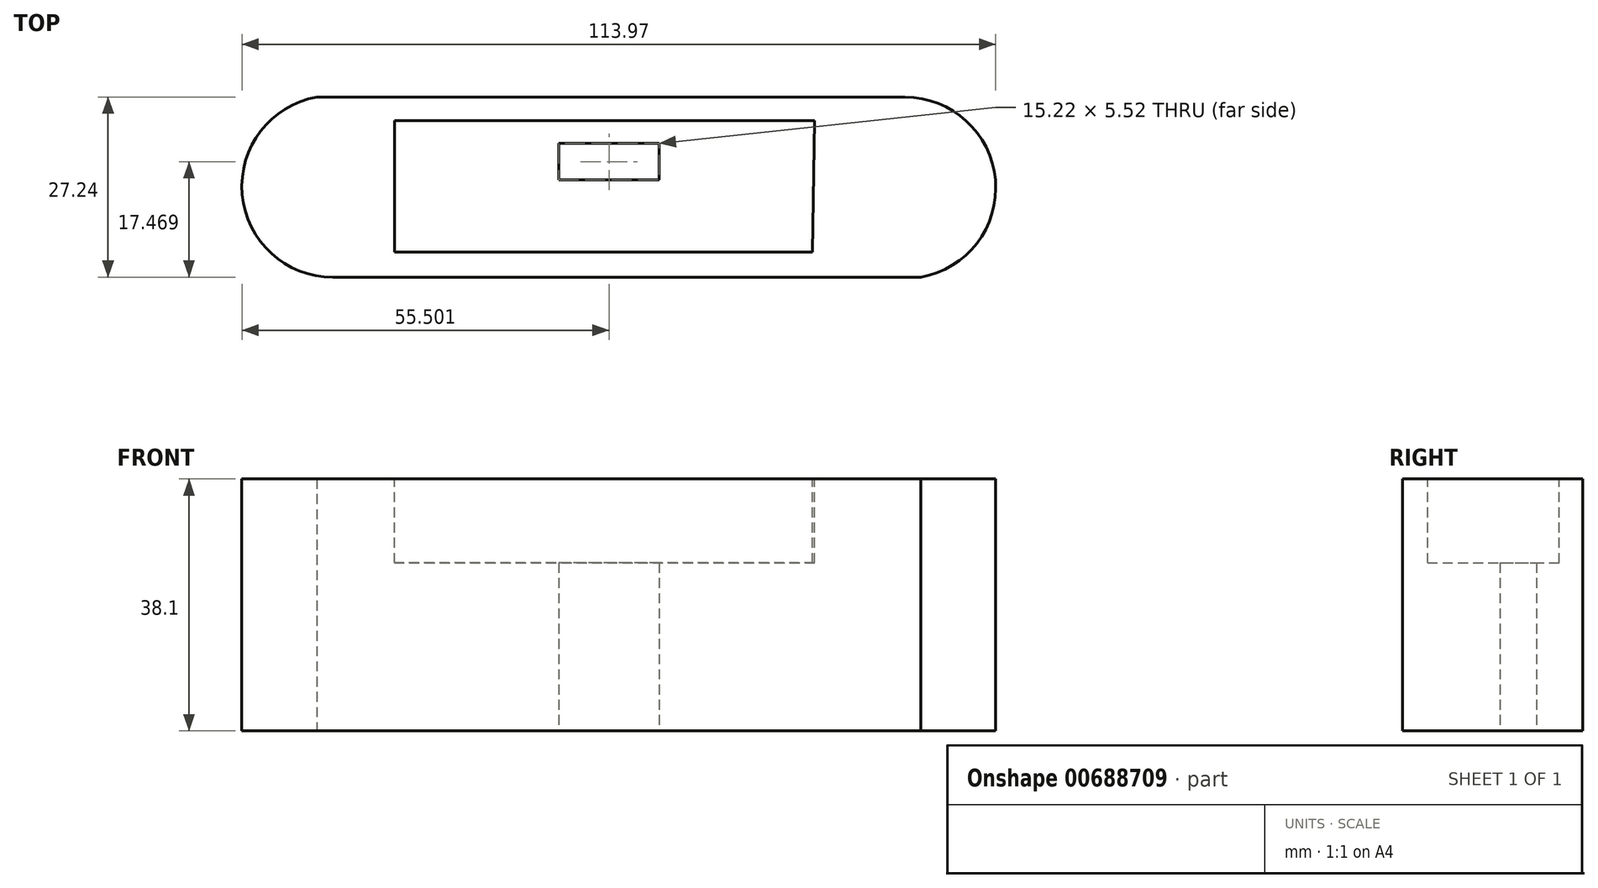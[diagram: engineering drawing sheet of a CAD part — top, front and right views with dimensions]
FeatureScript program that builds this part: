
annotation { "Feature Type Name" : "Feature", "Feature Type Description" : "" }
export const myFeature = defineFeature(function(context is Context, id is Id, definition is map)
    precondition{}
    {
        {
            var Q0;
            Q0=qCreatedBy(makeId("Top.planeOp"),FACE);
            var sketch = newSketch(context, id + "F0", { "sketchPlane" : qUnion([Q0])});
            skLineSegment(sketch, "E0", {"start": v(-44.14, 0) * mm, "end": v(44.76, 0) * mm});
            skArc(sketch, "E1", {"start": v(47.13, -27.24) * mm, "mid": v(58.43, -12.53) * mm, "end": v(44.76, 0) * mm});
            skLineSegment(sketch, "E2", {"start": v(47.13, -27.24) * mm, "end": v(-41.77, -27.24) * mm});
            skArc(sketch, "E3", {"start": v(-44.14, 0) * mm, "mid": v(-55.44, -14.71) * mm, "end": v(-41.77, -27.24) * mm});
            skSolve(sketch);
        }
        {
            var Q0;
            Q0=makeQuery(id+"F0.imprint","IMPRINT",FACE,{"disambiguationData":[TD([[makeQuery(id+"F0.imprint","IMPRINT",EDGE,{"derivedFrom":sQuery(id+"F0.wireOp",EDGE,"E0")}),-1.0]])]});
            extrude(context, id + "F1", {"entities" : qUnion([Q0]), "depth" : 12.7 * mm, "offsetDistance" : 25.4 * mm});
        }
        {
            var Q0;
            Q0=makeQuery(id+"F1.opExtrude","CAP_FACE",FACE,{"disambiguationData":[OSD([sQuery(id+"F0.wireOp",EDGE,"E0"),sQuery(id+"F0.wireOp",EDGE,"E1"),sQuery(id+"F0.wireOp",EDGE,"E2"),sQuery(id+"F0.wireOp",EDGE,"E3")])],"isStart":true});
            var sketch = newSketch(context, id + "F2", { "sketchPlane" : qUnion([Q0])});
            skLineSegment(sketch, "E4", {"start": v(-34.49, 27.24) * mm, "end": v(-34.49, 0) * mm});
            skSolve(sketch);
        }
        {
            var Q0;
            {var subQ0=sQuery(id+"F2.wireOp",EDGE,"E4");Q0=makeQuery(id+"F2.imprint","IMPRINT",FACE,{"disambiguationData":[TD([[makeQuery(id+"F2.imprint","IMPRINT",EDGE,{"derivedFrom":subQ0}),1.0]])]});}
            var sketch = newSketch(context, id + "F3", { "sketchPlane" : qUnion([Q0])});
            skLineSegment(sketch, "E5", {"start": v(31.5, 26.78) * mm, "end": v(31.5, 0) * mm});
            skSolve(sketch);
        }
        {
            var Q0;
            Q0=qSketchRegion(id+"F3",true);
            var Q1;
            {var subQ0=sQuery(id+"F2.wireOp",EDGE,"E4");Q1=makeQuery(id+"F2.imprint","IMPRINT",FACE,{"disambiguationData":[TD([[makeQuery(id+"F2.imprint","IMPRINT",EDGE,{"derivedFrom":subQ0}),1.0]])]});}
            extrude(context, id + "F4", {"entities" : qUnion([Q0, Q1]), "operationType" : NewBodyOperationType.ADD, "depth" : 25.4 * mm, "offsetDistance" : 25.4 * mm});
        }
        {
            var Q0;
            Q0=makeQuery(id+"F1.opExtrude","CAP_FACE",FACE,{"disambiguationData":[OSD([sQuery(id+"F0.wireOp",EDGE,"E0"),sQuery(id+"F0.wireOp",EDGE,"E1"),sQuery(id+"F0.wireOp",EDGE,"E2"),sQuery(id+"F0.wireOp",EDGE,"E3")])],"isStart":true});
            extrude(context, id + "F5", {"entities" : qUnion([Q0]), "operationType" : NewBodyOperationType.ADD, "depth" : 25.4 * mm, "offsetDistance" : 25.4 * mm});
        }
        {
            var Q0;
            Q0=makeQuery(id+"F1.opExtrude","CAP_FACE",FACE,{"disambiguationData":[OSD([sQuery(id+"F0.wireOp",EDGE,"E0"),sQuery(id+"F0.wireOp",EDGE,"E1"),sQuery(id+"F0.wireOp",EDGE,"E2"),sQuery(id+"F0.wireOp",EDGE,"E3")])],"isStart":false});
            var sketch = newSketch(context, id + "F6", { "sketchPlane" : qUnion([Q0])});
            skLineSegment(sketch, "E6", {"start": v(31.07, -3.55) * mm, "end": v(-32.43, -3.55) * mm});
            skLineSegment(sketch, "E7", {"start": v(-32.43, -3.55) * mm, "end": v(-32.43, -23.47) * mm});
            skLineSegment(sketch, "E8", {"start": v(-32.43, -23.47) * mm, "end": v(30.79, -23.47) * mm});
            skLineSegment(sketch, "E9", {"start": v(30.79, -23.47) * mm, "end": v(31.07, -3.55) * mm});
            skSolve(sketch);
        }
        {
            var Q0;
            Q0=qSketchRegion(id+"F6",true);
            extrude(context, id + "F7", {"entities" : qUnion([Q0]), "operationType" : NewBodyOperationType.REMOVE, "oppositeDirection" : true, "depth" : 12.7 * mm, "offsetDistance" : 25.4 * mm});
        }
        {
            var Q0;
            {var subQ0=sQuery(id+"F0.wireOp",EDGE,"E2");var subQ1=sQuery(id+"F0.wireOp",EDGE,"E1");var subQ2=sQuery(id+"F0.wireOp",EDGE,"E0");Q0=makeQuery(id+"F5.boolean.opBoolean","MERGE",FACE,{"derivedFrom":[makeQuery(id+"F4.opExtrude","CAP_FACE",FACE,{"disambiguationData":[OSD([subQ2,subQ1,subQ0,sQuery(id+"F2.wireOp",EDGE,"E4")])],"isStart":false}),makeQuery(id+"F5.opExtrude","CAP_FACE",FACE,{"disambiguationData":[OSD([subQ2,subQ1,subQ0,sQuery(id+"F0.wireOp",EDGE,"E3")])],"isStart":false})]});}
            var sketch = newSketch(context, id + "F8", { "sketchPlane" : qUnion([Q0])});
            skLineSegment(sketch, "E10", {"start": v(0, 12.53) * mm, "end": v(5.08, 12.53) * mm});
            skLineSegment(sketch, "E11", {"start": v(5.08, 12.53) * mm, "end": v(5.08, 7.01) * mm});
            skLineSegment(sketch, "E12", {"start": v(5.08, 7.01) * mm, "end": v(-5.06, 7.01) * mm});
            skLineSegment(sketch, "E13", {"start": v(-5.06, 7.01) * mm, "end": v(-5.06, 12.53) * mm});
            skPoint(sketch, "E13.endSnap0", {"position": v(2.54, 12.53) * mm});
            skLineSegment(sketch, "E14", {"start": v(-5.06, 12.53) * mm, "end": v(0, 12.53) * mm});
            skSolve(sketch);
        }
        {
            var Q0;
            Q0=qSketchRegion(id+"F8",true);
            extrude(context, id + "F9", {"entities" : qUnion([Q0]), "operationType" : NewBodyOperationType.REMOVE, "oppositeDirection" : true, "depth" : 25.4 * mm, "offsetDistance" : 25.4 * mm});
        }
        {
            var Q0;
            {var subQ0=sQuery(id+"F0.wireOp",EDGE,"E2");var subQ1=sQuery(id+"F0.wireOp",EDGE,"E1");var subQ2=sQuery(id+"F0.wireOp",EDGE,"E0");Q0=makeQuery(id+"F5.boolean.opBoolean","MERGE",FACE,{"derivedFrom":[makeQuery(id+"F4.opExtrude","CAP_FACE",FACE,{"disambiguationData":[OSD([subQ2,subQ1,subQ0,sQuery(id+"F2.wireOp",EDGE,"E4")])],"isStart":false}),makeQuery(id+"F5.opExtrude","CAP_FACE",FACE,{"disambiguationData":[OSD([subQ2,subQ1,subQ0,sQuery(id+"F0.wireOp",EDGE,"E3")])],"isStart":false})]});}
            var sketch = newSketch(context, id + "F10", { "sketchPlane" : qUnion([Q0])});
            skLineSegment(sketch, "E15", {"start": v(-5.06, 12.53) * mm, "end": v(-7.6, 12.53) * mm});
            skLineSegment(sketch, "E16", {"start": v(-7.6, 12.53) * mm, "end": v(-7.6, 7.01) * mm});
            skLineSegment(sketch, "E17", {"start": v(-7.6, 7.01) * mm, "end": v(-5.06, 7.01) * mm});
            skLineSegment(sketch, "E18", {"start": v(-5.06, 7.01) * mm, "end": v(5.08, 7.01) * mm});
            skLineSegment(sketch, "E19", {"start": v(5.08, 7.01) * mm, "end": v(7.62, 7.01) * mm});
            skLineSegment(sketch, "E20", {"start": v(7.62, 7.01) * mm, "end": v(7.62, 12.53) * mm});
            skLineSegment(sketch, "E21", {"start": v(7.62, 12.53) * mm, "end": v(5.08, 12.53) * mm});
            skSolve(sketch);
        }
        {
            var Q0;
            Q0=qSketchRegion(id+"F10",true);
            var Q1;
            Q1=makeQuery(id+"F10.imprint","IMPRINT",FACE,{"disambiguationData":[TD([[makeQuery(id+"F10.imprint","IMPRINT",EDGE,{"derivedFrom":sQuery(id+"F10.wireOp",EDGE,"E15")}),1.0]])]});
            var Q2;
            Q2=makeQuery(id+"F10.imprint","IMPRINT",FACE,{"disambiguationData":[TD([[makeQuery(id+"F10.imprint","IMPRINT",EDGE,{"derivedFrom":sQuery(id+"F10.wireOp",EDGE,"E19")}),1.0]])]});
            extrude(context, id + "F11", {"entities" : qUnion([Q0, Q1, Q2]), "operationType" : NewBodyOperationType.REMOVE, "oppositeDirection" : true, "depth" : 25.4 * mm, "offsetDistance" : 25.4 * mm});
        }
    });
